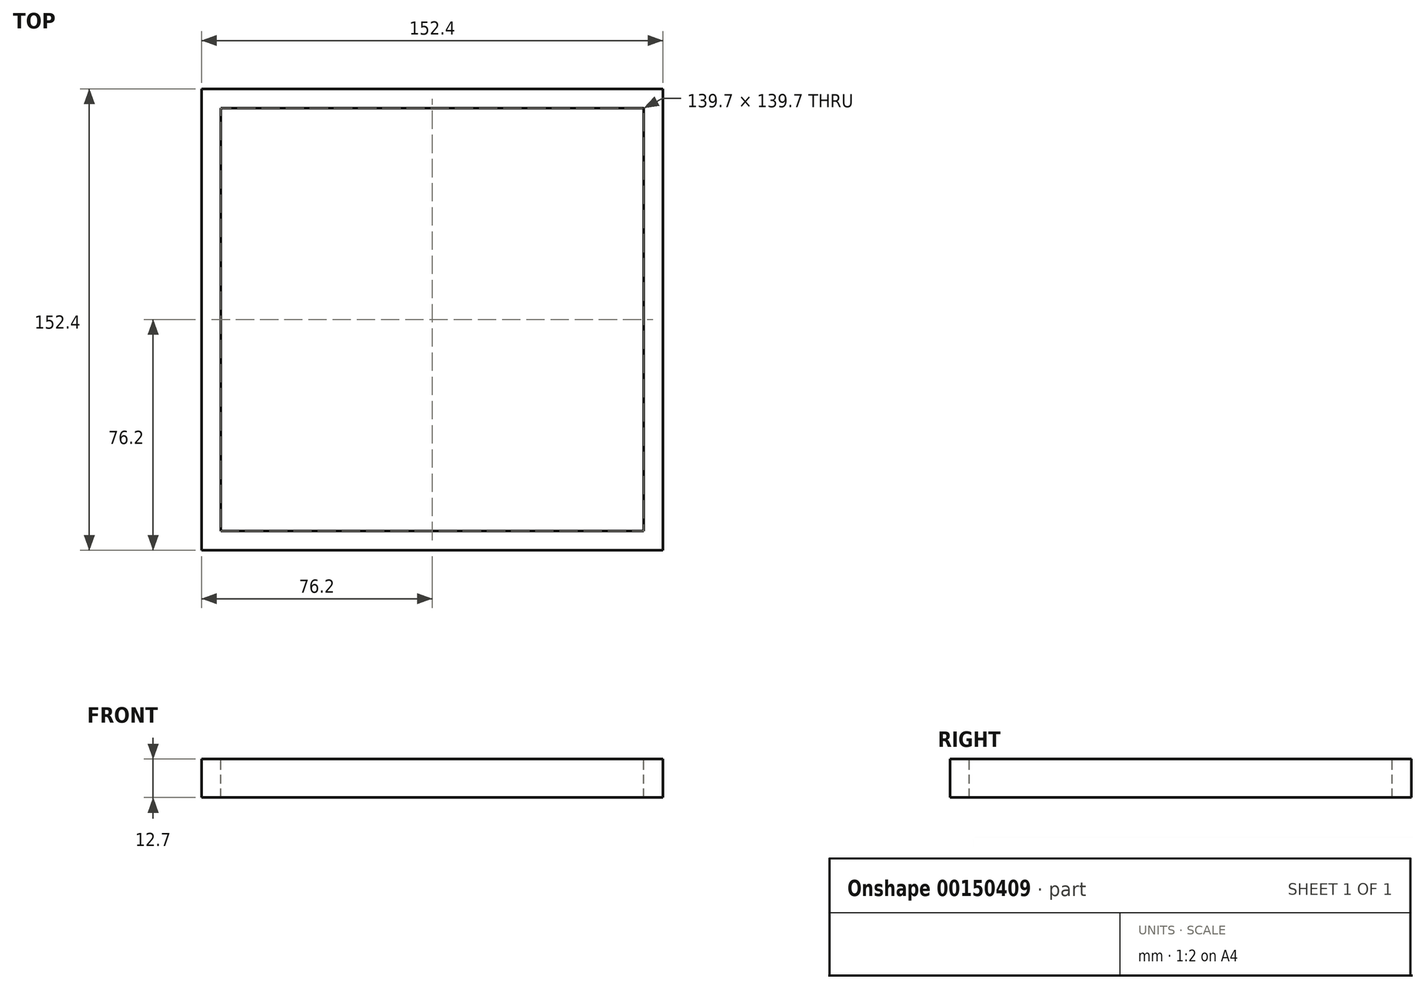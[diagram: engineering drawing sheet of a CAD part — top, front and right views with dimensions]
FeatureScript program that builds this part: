
annotation { "Feature Type Name" : "Feature", "Feature Type Description" : "" }
export const myFeature = defineFeature(function(context is Context, id is Id, definition is map)
    precondition{}
    {
        {
            var Q0;
            Q0=qCreatedBy(makeId("Top.planeOp"),FACE);
            var sketch = newSketch(context, id + "F0", { "sketchPlane" : qUnion([Q0])});
            skLineSegment(sketch, "E0.bottom", {"start": v(-150.5, 83.22) * mm, "end": v(149.21, 83.22) * mm});
            skLineSegment(sketch, "E0.top", {"start": v(-150.5, -86.74) * mm, "end": v(149.21, -86.74) * mm});
            skLineSegment(sketch, "E0.left", {"start": v(-150.5, 83.22) * mm, "end": v(-150.5, -86.74) * mm});
            skLineSegment(sketch, "E0.right", {"start": v(149.21, 83.22) * mm, "end": v(149.21, -86.74) * mm});
            skSolve(sketch);
        }
        {
            var Q0;
            Q0=makeQuery(id+"F0.imprint","IMPRINT",FACE,{"disambiguationData":[TD([[makeQuery(id+"F0.imprint","IMPRINT",EDGE,{"derivedFrom":sQuery(id+"F0.wireOp",EDGE,"E0.bottom")}),-1.0]])]});
            var sketch = newSketch(context, id + "F1", { "sketchPlane" : qUnion([Q0])});
            skLineSegment(sketch, "E1.bottom", {"start": v(88.4, 56.22) * mm, "end": v(139.2, 56.22) * mm});
            skLineSegment(sketch, "E1.top", {"start": v(88.4, 30.82) * mm, "end": v(139.2, 30.82) * mm});
            skLineSegment(sketch, "E1.left", {"start": v(88.4, 56.22) * mm, "end": v(88.4, 30.82) * mm});
            skLineSegment(sketch, "E1.right", {"start": v(139.2, 56.22) * mm, "end": v(139.2, 30.82) * mm});
            skLineSegment(sketch, "E2.bottom", {"start": v(88.4, 16.13) * mm, "end": v(139.2, 16.13) * mm});
            skLineSegment(sketch, "E2.top", {"start": v(88.4, -9.27) * mm, "end": v(139.2, -9.27) * mm});
            skLineSegment(sketch, "E2.left", {"start": v(88.4, 16.13) * mm, "end": v(88.4, -9.27) * mm});
            skLineSegment(sketch, "E2.right", {"start": v(139.2, 16.13) * mm, "end": v(139.2, -9.27) * mm});
            skLineSegment(sketch, "E3.bottom", {"start": v(88.4, -25.34) * mm, "end": v(139.2, -25.34) * mm});
            skLineSegment(sketch, "E3.top", {"start": v(88.4, -50.74) * mm, "end": v(139.2, -50.74) * mm});
            skLineSegment(sketch, "E3.left", {"start": v(88.4, -25.34) * mm, "end": v(88.4, -50.74) * mm});
            skLineSegment(sketch, "E3.right", {"start": v(139.2, -25.34) * mm, "end": v(139.2, -50.74) * mm});
            skLineSegment(sketch, "E4.MirrorCS", {"start": v(-88.4, 30.82) * mm, "end": v(-139.2, 30.82) * mm});
            skLineSegment(sketch, "E5.MirrorCS", {"start": v(-88.4, 56.22) * mm, "end": v(-88.4, 30.82) * mm});
            skLineSegment(sketch, "E6.MirrorCS", {"start": v(-88.4, 56.22) * mm, "end": v(-139.2, 56.22) * mm});
            skLineSegment(sketch, "E7.MirrorCS", {"start": v(-139.2, 56.22) * mm, "end": v(-139.2, 30.82) * mm});
            skLineSegment(sketch, "E8.MirrorCS", {"start": v(-139.2, 16.13) * mm, "end": v(-139.2, -9.27) * mm});
            skLineSegment(sketch, "E9.MirrorCS", {"start": v(-88.4, 16.13) * mm, "end": v(-88.4, -9.27) * mm});
            skLineSegment(sketch, "E10.MirrorCS", {"start": v(-88.4, 16.13) * mm, "end": v(-139.2, 16.13) * mm});
            skLineSegment(sketch, "E11.MirrorCS", {"start": v(-88.4, -9.27) * mm, "end": v(-139.2, -9.27) * mm});
            skLineSegment(sketch, "E12.MirrorCS", {"start": v(-88.4, -25.34) * mm, "end": v(-139.2, -25.34) * mm});
            skLineSegment(sketch, "E13.MirrorCS", {"start": v(-88.4, -25.34) * mm, "end": v(-88.4, -50.74) * mm});
            skLineSegment(sketch, "E14.MirrorCS", {"start": v(-88.4, -50.74) * mm, "end": v(-139.2, -50.74) * mm});
            skLineSegment(sketch, "E15.MirrorCS", {"start": v(-139.2, -25.34) * mm, "end": v(-139.2, -50.74) * mm});
            skSolve(sketch);
        }
        {
            var Q0;
            Q0=qCreatedBy(makeId("Top.planeOp"),FACE);
            var sketch = newSketch(context, id + "F2", { "sketchPlane" : qUnion([Q0])});
            skLineSegment(sketch, "E16.bottom", {"start": v(76.2, 76.2) * mm, "end": v(-76.2, 76.2) * mm});
            skLineSegment(sketch, "E16.top", {"start": v(76.2, -76.2) * mm, "end": v(-76.2, -76.2) * mm});
            skLineSegment(sketch, "E16.left", {"start": v(76.2, 76.2) * mm, "end": v(76.2, -76.2) * mm});
            skLineSegment(sketch, "E16.right", {"start": v(-76.2, 76.2) * mm, "end": v(-76.2, -76.2) * mm});
            skLineSegment(sketch, "E17.0", {"start": v(-69.85, 69.85) * mm, "end": v(-69.85, -69.85) * mm});
            skLineSegment(sketch, "E18.0", {"start": v(69.85, 69.85) * mm, "end": v(69.85, -69.85) * mm});
            skLineSegment(sketch, "E19.0", {"start": v(69.85, -69.85) * mm, "end": v(-69.85, -69.85) * mm});
            skLineSegment(sketch, "E20.0", {"start": v(69.85, 69.85) * mm, "end": v(-69.85, 69.85) * mm});
            skSolve(sketch);
        }
        {
            var Q0;
            Q0 = qSketchRegion(id + "F0", true);
            extrude(context, id + "F3", {"entities" : qUnion([Q0]), "depth" : 25.4 * mm});
        }
        {
            var Q0;
            Q0 = qSketchRegion(id + "F1", true);
            extrude(context, id + "F4", {"entities" : qUnion([Q0]), "operationType" : NewBodyOperationType.REMOVE, "depth" : 25.4 * mm});
        }
        {
            var Q0;
            Q0 = qSketchRegion(id + "F2", true);
            extrude(context, id + "F5", {"entities" : qUnion([Q0]), "operationType" : NewBodyOperationType.REMOVE, "depth" : 25.4 * mm});
        }
        {
            var Q0;
            Q0 = qSketchRegion(id + "F2", true);
            extrude(context, id + "F6", {"entities" : qUnion([Q0]), "oppositeDirection" : true, "depth" : 12.7 * mm});
        }
        {
            var Q0;
            Q0=makeQuery(id+"F5.boolean.opBoolean","SPLIT",BODY,{"disambiguationData":[OD(1.0)],"derivedFrom":makeQuery(id+"F3.opExtrude","SWEPT_BODY",BODY,{"disambiguationData":[OSD([sQuery(id+"F0.wireOp",EDGE,"E0.bottom"),sQuery(id+"F0.wireOp",EDGE,"E0.top"),sQuery(id+"F0.wireOp",EDGE,"E0.left"),sQuery(id+"F0.wireOp",EDGE,"E0.right")])]})});
            deleteBodies(context, id + "F7", {"entities" : qUnion([Q0])});
        }
    });
